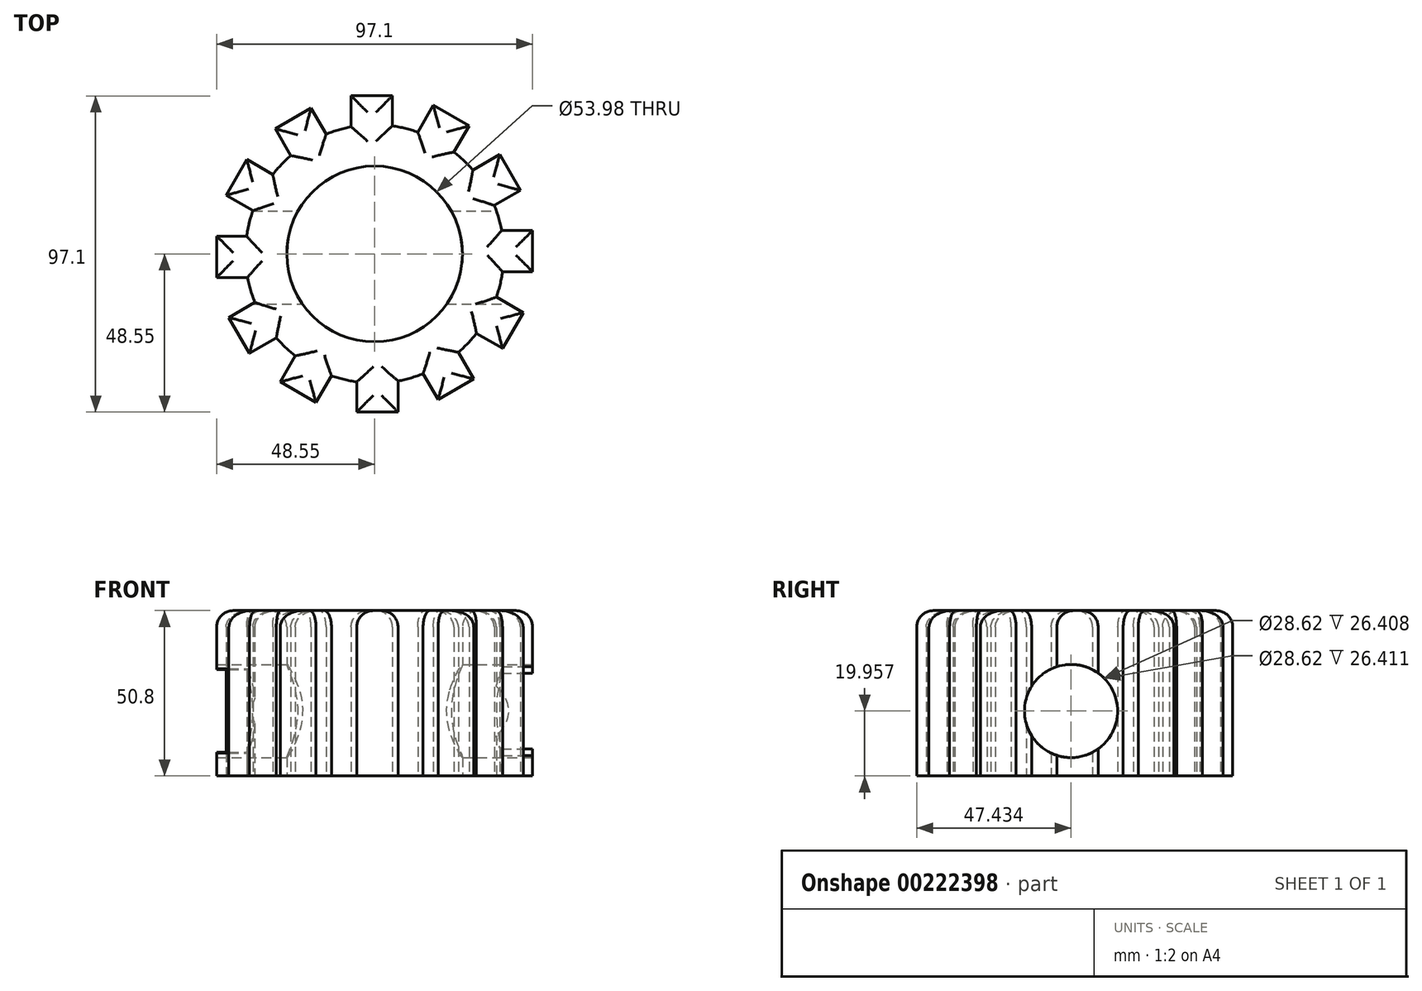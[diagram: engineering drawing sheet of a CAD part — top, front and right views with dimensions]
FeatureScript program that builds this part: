
annotation { "Feature Type Name" : "Feature", "Feature Type Description" : "" }
export const myFeature = defineFeature(function(context is Context, id is Id, definition is map)
    precondition{}
    {
        {
            var Q0;
            Q0=qCreatedBy(makeId("Top.planeOp"),FACE);
            var sketch = newSketch(context, id + "F0", { "sketchPlane" : qUnion([Q0])});
            skCircle(sketch, "E0", {"center": v(0, 0) * mm, "radius": 39.69 * mm});
            skCircle(sketch, "E1", {"center": v(0, 0) * mm, "radius": 26.99 * mm});
            skLineSegment(sketch, "E2.bottom", {"start": v(-7.21, 39.03) * mm, "end": v(5.49, 39.03) * mm});
            skLineSegment(sketch, "E2.top", {"start": v(-7.21, 48.55) * mm, "end": v(5.49, 48.55) * mm});
            skLineSegment(sketch, "E2.left", {"start": v(-7.21, 39.03) * mm, "end": v(-7.21, 48.55) * mm});
            skLineSegment(sketch, "E2.right", {"start": v(5.49, 39.03) * mm, "end": v(5.49, 48.55) * mm});
            skLineSegment(sketch, "E3.1.0", {"start": v(-14.76, 36.54) * mm, "end": v(-19.52, 44.8) * mm});
            skLineSegment(sketch, "E3.1.1", {"start": v(-25.76, 30.2) * mm, "end": v(-30.52, 38.44) * mm});
            skLineSegment(sketch, "E3.1.2", {"start": v(-30.52, 38.44) * mm, "end": v(-19.52, 44.8) * mm});
            skLineSegment(sketch, "E3.1.3", {"start": v(-25.76, 30.2) * mm, "end": v(-14.76, 36.54) * mm});
            skLineSegment(sketch, "E3.2.0", {"start": v(-31.05, 24.26) * mm, "end": v(-39.3, 29.03) * mm});
            skLineSegment(sketch, "E3.2.1", {"start": v(-37.4, 13.27) * mm, "end": v(-45.65, 18.03) * mm});
            skLineSegment(sketch, "E3.2.2", {"start": v(-45.65, 18.03) * mm, "end": v(-39.3, 29.03) * mm});
            skLineSegment(sketch, "E3.2.3", {"start": v(-37.4, 13.27) * mm, "end": v(-31.05, 24.26) * mm});
            skLineSegment(sketch, "E3.3.0", {"start": v(-39.03, 5.49) * mm, "end": v(-48.55, 5.49) * mm});
            skLineSegment(sketch, "E3.3.1", {"start": v(-39.03, -7.21) * mm, "end": v(-48.55, -7.21) * mm});
            skLineSegment(sketch, "E3.3.2", {"start": v(-48.55, -7.21) * mm, "end": v(-48.55, 5.49) * mm});
            skLineSegment(sketch, "E3.3.3", {"start": v(-39.03, -7.21) * mm, "end": v(-39.03, 5.49) * mm});
            skLineSegment(sketch, "E3.4.0", {"start": v(-36.54, -14.76) * mm, "end": v(-44.8, -19.52) * mm});
            skLineSegment(sketch, "E3.4.1", {"start": v(-30.2, -25.76) * mm, "end": v(-38.44, -30.52) * mm});
            skLineSegment(sketch, "E3.4.2", {"start": v(-38.44, -30.52) * mm, "end": v(-44.8, -19.52) * mm});
            skLineSegment(sketch, "E3.4.3", {"start": v(-30.2, -25.76) * mm, "end": v(-36.54, -14.76) * mm});
            skLineSegment(sketch, "E3.5.0", {"start": v(-24.26, -31.05) * mm, "end": v(-29.03, -39.3) * mm});
            skLineSegment(sketch, "E3.5.1", {"start": v(-13.27, -37.4) * mm, "end": v(-18.03, -45.65) * mm});
            skLineSegment(sketch, "E3.5.2", {"start": v(-18.03, -45.65) * mm, "end": v(-29.03, -39.3) * mm});
            skLineSegment(sketch, "E3.5.3", {"start": v(-13.27, -37.4) * mm, "end": v(-24.26, -31.05) * mm});
            skLineSegment(sketch, "E3.6.0", {"start": v(-5.49, -39.03) * mm, "end": v(-5.49, -48.55) * mm});
            skLineSegment(sketch, "E3.6.1", {"start": v(7.21, -39.03) * mm, "end": v(7.21, -48.55) * mm});
            skLineSegment(sketch, "E3.6.2", {"start": v(7.21, -48.55) * mm, "end": v(-5.49, -48.55) * mm});
            skLineSegment(sketch, "E3.6.3", {"start": v(7.21, -39.03) * mm, "end": v(-5.49, -39.03) * mm});
            skLineSegment(sketch, "E3.7.0", {"start": v(14.76, -36.54) * mm, "end": v(19.52, -44.8) * mm});
            skLineSegment(sketch, "E3.7.1", {"start": v(25.76, -30.2) * mm, "end": v(30.52, -38.44) * mm});
            skLineSegment(sketch, "E3.7.2", {"start": v(30.52, -38.44) * mm, "end": v(19.52, -44.8) * mm});
            skLineSegment(sketch, "E3.7.3", {"start": v(25.76, -30.2) * mm, "end": v(14.76, -36.54) * mm});
            skLineSegment(sketch, "E3.8.0", {"start": v(31.05, -24.26) * mm, "end": v(39.3, -29.03) * mm});
            skLineSegment(sketch, "E3.8.1", {"start": v(37.4, -13.27) * mm, "end": v(45.65, -18.03) * mm});
            skLineSegment(sketch, "E3.8.2", {"start": v(45.65, -18.03) * mm, "end": v(39.3, -29.03) * mm});
            skLineSegment(sketch, "E3.8.3", {"start": v(37.4, -13.27) * mm, "end": v(31.05, -24.26) * mm});
            skLineSegment(sketch, "E3.9.0", {"start": v(39.03, -5.49) * mm, "end": v(48.55, -5.49) * mm});
            skLineSegment(sketch, "E3.9.1", {"start": v(39.03, 7.21) * mm, "end": v(48.55, 7.21) * mm});
            skLineSegment(sketch, "E3.9.2", {"start": v(48.55, 7.21) * mm, "end": v(48.55, -5.49) * mm});
            skLineSegment(sketch, "E3.9.3", {"start": v(39.03, 7.21) * mm, "end": v(39.03, -5.49) * mm});
            skLineSegment(sketch, "E3.10.0", {"start": v(36.54, 14.76) * mm, "end": v(44.8, 19.52) * mm});
            skLineSegment(sketch, "E3.10.1", {"start": v(30.2, 25.76) * mm, "end": v(38.44, 30.52) * mm});
            skLineSegment(sketch, "E3.10.2", {"start": v(38.44, 30.52) * mm, "end": v(44.8, 19.52) * mm});
            skLineSegment(sketch, "E3.10.3", {"start": v(30.2, 25.76) * mm, "end": v(36.54, 14.76) * mm});
            skLineSegment(sketch, "E3.11.0", {"start": v(24.26, 31.05) * mm, "end": v(29.03, 39.3) * mm});
            skLineSegment(sketch, "E3.11.1", {"start": v(13.27, 37.4) * mm, "end": v(18.03, 45.65) * mm});
            skLineSegment(sketch, "E3.11.2", {"start": v(18.03, 45.65) * mm, "end": v(29.03, 39.3) * mm});
            skLineSegment(sketch, "E3.11.3", {"start": v(13.27, 37.4) * mm, "end": v(24.26, 31.05) * mm});
            skSolve(sketch);
        }
        {
            var Q0;
            {var subQ0=sQuery(id+"F0.wireOp",EDGE,"E3.10.1");Q0=makeQuery(id+"F0.imprint","IMPRINT",FACE,{"disambiguationData":[TD([[makeQuery(id+"F0.imprint","IMPRINT",EDGE,{"derivedFrom":subQ0}),-1.0]])]});}
            var Q1;
            {var subQ0=sQuery(id+"F0.wireOp",EDGE,"E3.11.1");Q1=makeQuery(id+"F0.imprint","IMPRINT",FACE,{"disambiguationData":[TD([[makeQuery(id+"F0.imprint","IMPRINT",EDGE,{"derivedFrom":subQ0}),-1.0]])]});}
            var Q2;
            {var subQ4=sQuery(id+"F0.wireOp",EDGE,"E2.top");Q2=makeQuery(id+"F0.imprint","IMPRINT",FACE,{"disambiguationData":[TD([[makeQuery(id+"F0.imprint","IMPRINT",EDGE,{"derivedFrom":subQ4}),-1.0]])]});}
            var Q3;
            {var subQ0=sQuery(id+"F0.wireOp",EDGE,"E3.2.1");Q3=makeQuery(id+"F0.imprint","IMPRINT",FACE,{"disambiguationData":[TD([[makeQuery(id+"F0.imprint","IMPRINT",EDGE,{"derivedFrom":subQ0}),-1.0]])]});}
            var Q4;
            {var subQ0=sQuery(id+"F0.wireOp",EDGE,"E3.3.1");Q4=makeQuery(id+"F0.imprint","IMPRINT",FACE,{"disambiguationData":[TD([[makeQuery(id+"F0.imprint","IMPRINT",EDGE,{"derivedFrom":subQ0}),-1.0]])]});}
            var Q5;
            {var subQ0=sQuery(id+"F0.wireOp",EDGE,"E3.4.1");Q5=makeQuery(id+"F0.imprint","IMPRINT",FACE,{"disambiguationData":[TD([[makeQuery(id+"F0.imprint","IMPRINT",EDGE,{"derivedFrom":subQ0}),-1.0]])]});}
            var Q6;
            {var subQ0=sQuery(id+"F0.wireOp",EDGE,"E3.5.1");Q6=makeQuery(id+"F0.imprint","IMPRINT",FACE,{"disambiguationData":[TD([[makeQuery(id+"F0.imprint","IMPRINT",EDGE,{"derivedFrom":subQ0}),-1.0]])]});}
            var Q7;
            {var subQ0=sQuery(id+"F0.wireOp",EDGE,"E3.6.1");Q7=makeQuery(id+"F0.imprint","IMPRINT",FACE,{"disambiguationData":[TD([[makeQuery(id+"F0.imprint","IMPRINT",EDGE,{"derivedFrom":subQ0}),-1.0]])]});}
            var Q8;
            {var subQ0=sQuery(id+"F0.wireOp",EDGE,"E3.7.1");Q8=makeQuery(id+"F0.imprint","IMPRINT",FACE,{"disambiguationData":[TD([[makeQuery(id+"F0.imprint","IMPRINT",EDGE,{"derivedFrom":subQ0}),-1.0]])]});}
            var Q9;
            {var subQ0=sQuery(id+"F0.wireOp",EDGE,"E3.8.1");Q9=makeQuery(id+"F0.imprint","IMPRINT",FACE,{"disambiguationData":[TD([[makeQuery(id+"F0.imprint","IMPRINT",EDGE,{"derivedFrom":subQ0}),-1.0]])]});}
            var Q10;
            {var subQ0=sQuery(id+"F0.wireOp",EDGE,"E3.9.1");Q10=makeQuery(id+"F0.imprint","IMPRINT",FACE,{"disambiguationData":[TD([[makeQuery(id+"F0.imprint","IMPRINT",EDGE,{"derivedFrom":subQ0}),-1.0]])]});}
            var Q11;
            {var subQ0=sQuery(id+"F0.wireOp",EDGE,"E3.10.3");Q11=makeQuery(id+"F0.imprint","IMPRINT",FACE,{"disambiguationData":[TD([[makeQuery(id+"F0.imprint","IMPRINT",EDGE,{"derivedFrom":subQ0}),1.0]])]});}
            var Q12;
            {var subQ0=sQuery(id+"F0.wireOp",EDGE,"E3.11.3");Q12=makeQuery(id+"F0.imprint","IMPRINT",FACE,{"disambiguationData":[TD([[makeQuery(id+"F0.imprint","IMPRINT",EDGE,{"derivedFrom":subQ0}),1.0]])]});}
            var Q13;
            {var subQ0=sQuery(id+"F0.wireOp",EDGE,"E2.bottom");Q13=makeQuery(id+"F0.imprint","IMPRINT",FACE,{"disambiguationData":[TD([[makeQuery(id+"F0.imprint","IMPRINT",EDGE,{"derivedFrom":subQ0}),1.0]])]});}
            var Q14;
            {var subQ0=sQuery(id+"F0.wireOp",EDGE,"E3.1.3");Q14=makeQuery(id+"F0.imprint","IMPRINT",FACE,{"disambiguationData":[TD([[makeQuery(id+"F0.imprint","IMPRINT",EDGE,{"derivedFrom":subQ0}),1.0]])]});}
            var Q15;
            {var subQ0=sQuery(id+"F0.wireOp",EDGE,"E3.2.3");Q15=makeQuery(id+"F0.imprint","IMPRINT",FACE,{"disambiguationData":[TD([[makeQuery(id+"F0.imprint","IMPRINT",EDGE,{"derivedFrom":subQ0}),1.0]])]});}
            var Q16;
            {var subQ0=sQuery(id+"F0.wireOp",EDGE,"E3.3.3");Q16=makeQuery(id+"F0.imprint","IMPRINT",FACE,{"disambiguationData":[TD([[makeQuery(id+"F0.imprint","IMPRINT",EDGE,{"derivedFrom":subQ0}),1.0]])]});}
            var Q17;
            {var subQ0=sQuery(id+"F0.wireOp",EDGE,"E3.4.3");Q17=makeQuery(id+"F0.imprint","IMPRINT",FACE,{"disambiguationData":[TD([[makeQuery(id+"F0.imprint","IMPRINT",EDGE,{"derivedFrom":subQ0}),1.0]])]});}
            var Q18;
            {var subQ0=sQuery(id+"F0.wireOp",EDGE,"E3.5.3");Q18=makeQuery(id+"F0.imprint","IMPRINT",FACE,{"disambiguationData":[TD([[makeQuery(id+"F0.imprint","IMPRINT",EDGE,{"derivedFrom":subQ0}),1.0]])]});}
            var Q19;
            {var subQ0=sQuery(id+"F0.wireOp",EDGE,"E3.6.3");Q19=makeQuery(id+"F0.imprint","IMPRINT",FACE,{"disambiguationData":[TD([[makeQuery(id+"F0.imprint","IMPRINT",EDGE,{"derivedFrom":subQ0}),1.0]])]});}
            var Q20;
            {var subQ0=sQuery(id+"F0.wireOp",EDGE,"E3.7.3");Q20=makeQuery(id+"F0.imprint","IMPRINT",FACE,{"disambiguationData":[TD([[makeQuery(id+"F0.imprint","IMPRINT",EDGE,{"derivedFrom":subQ0}),1.0]])]});}
            var Q21;
            {var subQ0=sQuery(id+"F0.wireOp",EDGE,"E3.8.3");Q21=makeQuery(id+"F0.imprint","IMPRINT",FACE,{"disambiguationData":[TD([[makeQuery(id+"F0.imprint","IMPRINT",EDGE,{"derivedFrom":subQ0}),1.0]])]});}
            var Q22;
            {var subQ0=sQuery(id+"F0.wireOp",EDGE,"E3.9.3");Q22=makeQuery(id+"F0.imprint","IMPRINT",FACE,{"disambiguationData":[TD([[makeQuery(id+"F0.imprint","IMPRINT",EDGE,{"derivedFrom":subQ0}),1.0]])]});}
            var Q23;
            Q23=makeQuery(id+"F0.imprint","IMPRINT",FACE,{"disambiguationData":[TD([[makeQuery(id+"F0.imprint","IMPRINT",EDGE,{"derivedFrom":sQuery(id+"F0.wireOp",EDGE,"E1")}),-1.0]])]});
            var Q24;
            {var subQ0=sQuery(id+"F0.wireOp",EDGE,"E3.1.1");Q24=makeQuery(id+"F0.imprint","IMPRINT",FACE,{"disambiguationData":[TD([[makeQuery(id+"F0.imprint","IMPRINT",EDGE,{"derivedFrom":subQ0}),-1.0]])]});}
            extrude(context, id + "F1", {"entities" : qUnion([Q0, Q1, Q2, Q3, Q4, Q5, Q6, Q7, Q8, Q9, Q10, Q11, Q12, Q13, Q14, Q15, Q16, Q17, Q18, Q19, Q20, Q21, Q22, Q23, Q24]), "depth" : 50.8 * mm});
        }
        {
            var Q0;
            Q0=makeQuery(id+"F1.opExtrude","CAP_EDGE",EDGE,{"disambiguationData":[OSD([sQuery(id+"F0.wireOp",EDGE,"E3.10.0")])],"isStart":false});
            var Q1;
            Q1=makeQuery(id+"F1.opExtrude","CAP_EDGE",EDGE,{"disambiguationData":[OSD([sQuery(id+"F0.wireOp",EDGE,"E3.10.1")])],"isStart":false});
            var Q2;
            Q2=makeQuery(id+"F1.opExtrude","CAP_EDGE",EDGE,{"disambiguationData":[OSD([sQuery(id+"F0.wireOp",EDGE,"E3.10.2")])],"isStart":false});
            var Q3;
            Q3=makeQuery(id+"F1.opExtrude","CAP_EDGE",EDGE,{"disambiguationData":[OSD([sQuery(id+"F0.wireOp",EDGE,"E3.9.1")])],"isStart":false});
            var Q4;
            Q4=makeQuery(id+"F1.opExtrude","CAP_EDGE",EDGE,{"disambiguationData":[OSD([sQuery(id+"F0.wireOp",EDGE,"E3.9.2")])],"isStart":false});
            var Q5;
            Q5=makeQuery(id+"F1.opExtrude","CAP_EDGE",EDGE,{"disambiguationData":[OSD([sQuery(id+"F0.wireOp",EDGE,"E3.9.0")])],"isStart":false});
            var Q6;
            Q6=makeQuery(id+"F1.opExtrude","CAP_FACE",FACE,{"disambiguationData":[OSD([sQuery(id+"F0.wireOp",EDGE,"E0"),sQuery(id+"F0.wireOp",EDGE,"E1"),sQuery(id+"F0.wireOp",EDGE,"E2.top"),sQuery(id+"F0.wireOp",EDGE,"E2.left"),sQuery(id+"F0.wireOp",EDGE,"E2.right"),sQuery(id+"F0.wireOp",EDGE,"E3.1.0"),sQuery(id+"F0.wireOp",EDGE,"E3.1.1"),sQuery(id+"F0.wireOp",EDGE,"E3.1.2"),sQuery(id+"F0.wireOp",EDGE,"E3.2.0"),sQuery(id+"F0.wireOp",EDGE,"E3.2.1"),sQuery(id+"F0.wireOp",EDGE,"E3.2.2"),sQuery(id+"F0.wireOp",EDGE,"E3.3.0"),sQuery(id+"F0.wireOp",EDGE,"E3.3.1"),sQuery(id+"F0.wireOp",EDGE,"E3.3.2"),sQuery(id+"F0.wireOp",EDGE,"E3.4.0"),sQuery(id+"F0.wireOp",EDGE,"E3.4.1"),sQuery(id+"F0.wireOp",EDGE,"E3.4.2"),sQuery(id+"F0.wireOp",EDGE,"E3.5.0"),sQuery(id+"F0.wireOp",EDGE,"E3.5.1"),sQuery(id+"F0.wireOp",EDGE,"E3.5.2"),sQuery(id+"F0.wireOp",EDGE,"E3.6.0"),sQuery(id+"F0.wireOp",EDGE,"E3.6.1"),sQuery(id+"F0.wireOp",EDGE,"E3.6.2"),sQuery(id+"F0.wireOp",EDGE,"E3.7.0"),sQuery(id+"F0.wireOp",EDGE,"E3.7.1"),sQuery(id+"F0.wireOp",EDGE,"E3.7.2"),sQuery(id+"F0.wireOp",EDGE,"E3.8.0"),sQuery(id+"F0.wireOp",EDGE,"E3.8.1"),sQuery(id+"F0.wireOp",EDGE,"E3.8.2"),sQuery(id+"F0.wireOp",EDGE,"E3.9.0"),sQuery(id+"F0.wireOp",EDGE,"E3.9.1"),sQuery(id+"F0.wireOp",EDGE,"E3.9.2"),sQuery(id+"F0.wireOp",EDGE,"E3.10.0"),sQuery(id+"F0.wireOp",EDGE,"E3.10.1"),sQuery(id+"F0.wireOp",EDGE,"E3.10.2"),sQuery(id+"F0.wireOp",EDGE,"E3.11.0"),sQuery(id+"F0.wireOp",EDGE,"E3.11.1"),sQuery(id+"F0.wireOp",EDGE,"E3.11.2")])],"isStart":false});
            fillet(context, id + "F2", {"entities" : qUnion([Q0, Q1, Q2, Q3, Q4, Q5, Q6]), "radius" : 5.08 * mm, "tangentPropagation" : true, "allowEdgeOverflow" : false});
        }
        {
            var Q0;
            Q0=makeQuery(id+"F1.opExtrude","SWEPT_FACE",FACE,{"disambiguationData":[OSD([sQuery(id+"F0.wireOp",EDGE,"E3.9.2")])]});
            var sketch = newSketch(context, id + "F3", { "sketchPlane" : qUnion([Q0])});
            skCircle(sketch, "E4", {"center": v(-1.12, 19.96) * mm, "radius": 14.3 * mm});
            skSolve(sketch);
        }
        {
            var Q0;
            {var subQ0=sQuery(id+"F3.wireOp",EDGE,"E4");var subQ1=makeQuery(id+"F1.opExtrude","SWEPT_EDGE",EDGE,{"disambiguationData":[OSD([sQuery(id+"F0.wireOp",EDGE,"E3.9.0"),sQuery(id+"F0.wireOp",EDGE,"E3.9.2")])]});var subQ2=makeQuery(id+"F3.imprint","INTERSECT",VERTEX,{"disambiguationData":[OD(0.0)],"derivedFrom":[subQ1,subQ0]});Q0=makeQuery(id+"F3.imprint","IMPRINT",FACE,{"disambiguationData":[TD([[makeQuery(id+"F3.imprint","IMPRINT",EDGE,{"disambiguationData":[TD([[subQ2,-1.0]])],"derivedFrom":subQ0}),1.0]])]});}
            var Q1;
            {var subQ0=sQuery(id+"F3.wireOp",EDGE,"E4");var subQ1=sQuery(id+"F0.wireOp",EDGE,"E3.9.2");var subQ2=makeQuery(id+"F1.opExtrude","SWEPT_EDGE",EDGE,{"disambiguationData":[OSD([sQuery(id+"F0.wireOp",EDGE,"E3.9.0"),subQ1])]});var subQ3=makeQuery(id+"F3.imprint","INTERSECT",VERTEX,{"disambiguationData":[OD(0.0)],"derivedFrom":[subQ2,subQ0]});Q1=makeQuery(id+"F3.imprint","IMPRINT",FACE,{"disambiguationData":[TD([[makeQuery(id+"F3.imprint","IMPRINT",EDGE,{"disambiguationData":[TD([[subQ3,1.0]])],"derivedFrom":subQ0}),1.0]])]});}
            var Q2;
            {var subQ0=sQuery(id+"F3.wireOp",EDGE,"E4");var subQ1=makeQuery(id+"F1.opExtrude","SWEPT_EDGE",EDGE,{"disambiguationData":[OSD([sQuery(id+"F0.wireOp",EDGE,"E3.9.1"),sQuery(id+"F0.wireOp",EDGE,"E3.9.2")])]});var subQ2=makeQuery(id+"F3.imprint","INTERSECT",VERTEX,{"disambiguationData":[OD(0.0)],"derivedFrom":[subQ1,subQ0]});Q2=makeQuery(id+"F3.imprint","IMPRINT",FACE,{"disambiguationData":[TD([[makeQuery(id+"F3.imprint","IMPRINT",EDGE,{"disambiguationData":[TD([[subQ2,1.0]])],"derivedFrom":subQ0}),1.0]])]});}
            var Q3;
            Q3=sQuery(id+"F3.wireOp",EDGE,"E4");
            extrude(context, id + "F4", {"entities" : qUnion([Q0, Q1, Q2]), "operationType" : NewBodyOperationType.REMOVE, "surfaceEntities" : qUnion([Q3]), "oppositeDirection" : true, "depth" : 25.4 * mm, "offsetDistance" : 25.4 * mm});
        }
        {
            var Q0;
            {var subQ0=sQuery(id+"F3.wireOp",EDGE,"E4");var subQ1=makeQuery(id+"F1.opExtrude","SWEPT_EDGE",EDGE,{"disambiguationData":[OSD([sQuery(id+"F0.wireOp",EDGE,"E3.9.0"),sQuery(id+"F0.wireOp",EDGE,"E3.9.2")])]});var subQ2=makeQuery(id+"F3.imprint","INTERSECT",VERTEX,{"disambiguationData":[OD(0.0)],"derivedFrom":[subQ1,subQ0]});Q0=makeQuery(id+"F3.imprint","IMPRINT",FACE,{"disambiguationData":[TD([[makeQuery(id+"F3.imprint","IMPRINT",EDGE,{"disambiguationData":[TD([[subQ2,-1.0]])],"derivedFrom":subQ0}),1.0]])]});}
            var Q1;
            {var subQ0=sQuery(id+"F3.wireOp",EDGE,"E4");var subQ1=sQuery(id+"F0.wireOp",EDGE,"E3.9.2");var subQ2=makeQuery(id+"F1.opExtrude","SWEPT_EDGE",EDGE,{"disambiguationData":[OSD([sQuery(id+"F0.wireOp",EDGE,"E3.9.0"),subQ1])]});var subQ3=makeQuery(id+"F3.imprint","INTERSECT",VERTEX,{"disambiguationData":[OD(0.0)],"derivedFrom":[subQ2,subQ0]});Q1=makeQuery(id+"F3.imprint","IMPRINT",FACE,{"disambiguationData":[TD([[makeQuery(id+"F3.imprint","IMPRINT",EDGE,{"disambiguationData":[TD([[subQ3,1.0]])],"derivedFrom":subQ0}),1.0]])]});}
            var Q2;
            {var subQ0=sQuery(id+"F3.wireOp",EDGE,"E4");var subQ1=makeQuery(id+"F1.opExtrude","SWEPT_EDGE",EDGE,{"disambiguationData":[OSD([sQuery(id+"F0.wireOp",EDGE,"E3.9.1"),sQuery(id+"F0.wireOp",EDGE,"E3.9.2")])]});var subQ2=makeQuery(id+"F3.imprint","INTERSECT",VERTEX,{"disambiguationData":[OD(0.0)],"derivedFrom":[subQ1,subQ0]});Q2=makeQuery(id+"F3.imprint","IMPRINT",FACE,{"disambiguationData":[TD([[makeQuery(id+"F3.imprint","IMPRINT",EDGE,{"disambiguationData":[TD([[subQ2,1.0]])],"derivedFrom":subQ0}),1.0]])]});}
            extrude(context, id + "F5", {"entities" : qUnion([Q0, Q1, Q2]), "operationType" : NewBodyOperationType.REMOVE, "endBound" : BoundingType.THROUGH_ALL, "oppositeDirection" : true, "depth" : 25.4 * mm});
        }
    });
